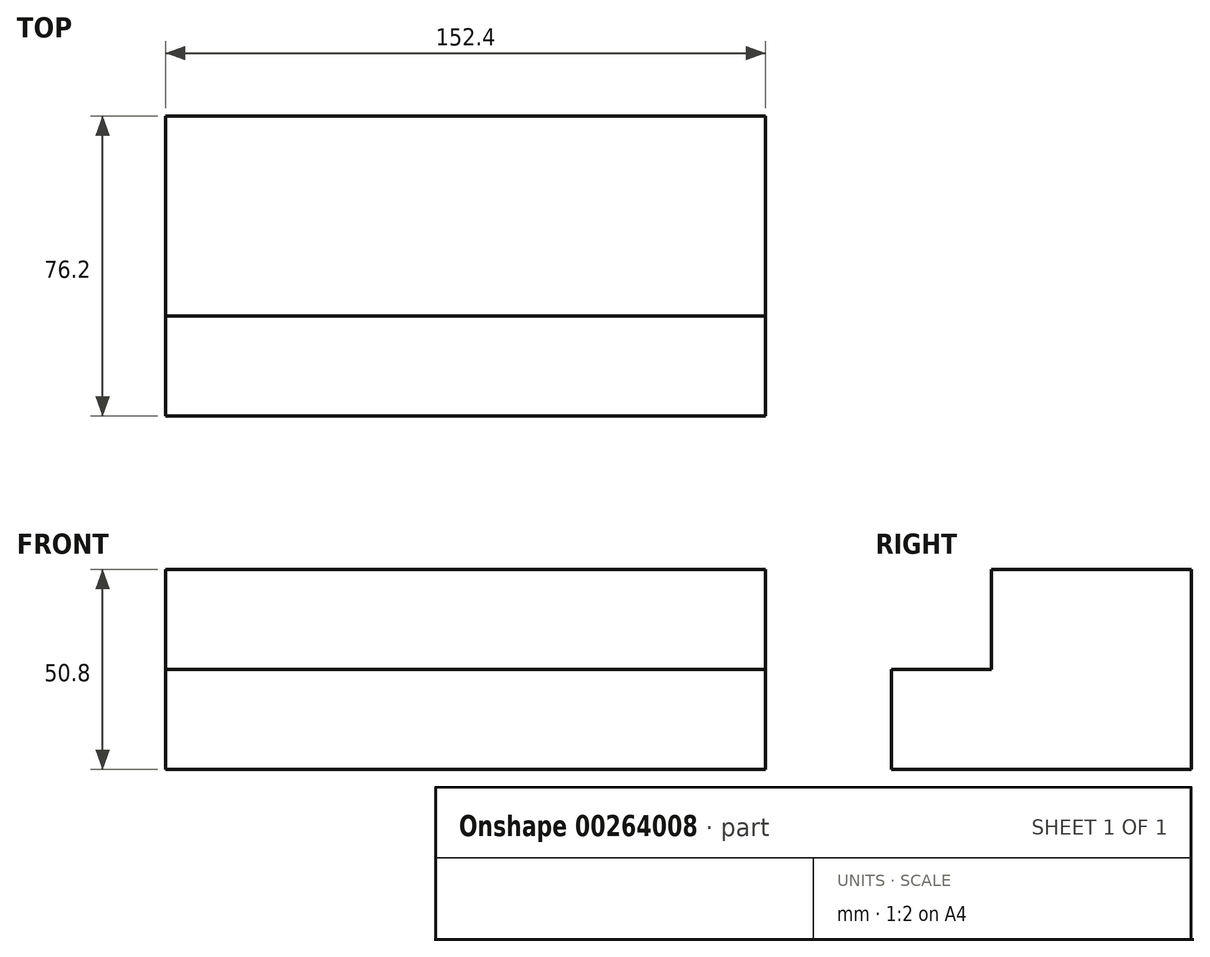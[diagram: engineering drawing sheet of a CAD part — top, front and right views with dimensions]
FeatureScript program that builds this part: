
annotation { "Feature Type Name" : "Feature", "Feature Type Description" : "" }
export const myFeature = defineFeature(function(context is Context, id is Id, definition is map)
    precondition{}
    {
        {
            var Q0;
            Q0=qCreatedBy(makeId("Right.planeOp"),FACE);
            var sketch = newSketch(context, id + "F0", { "sketchPlane" : qUnion([Q0])});
            skLineSegment(sketch, "E0", {"start": v(0, 0) * mm, "end": v(50.8, 0) * mm});
            skLineSegment(sketch, "E1", {"start": v(50.8, 0) * mm, "end": v(50.8, -50.8) * mm});
            skLineSegment(sketch, "E2", {"start": v(50.8, -50.8) * mm, "end": v(0, -50.8) * mm});
            skLineSegment(sketch, "E3", {"start": v(0, -50.8) * mm, "end": v(-25.4, -50.8) * mm});
            skLineSegment(sketch, "E4", {"start": v(-25.4, -50.8) * mm, "end": v(-25.4, -25.4) * mm});
            skLineSegment(sketch, "E5", {"start": v(-25.4, -25.4) * mm, "end": v(0, -25.4) * mm});
            skLineSegment(sketch, "E6", {"start": v(0, -25.4) * mm, "end": v(0, 0) * mm});
            skSolve(sketch);
        }
        {
            var Q0;
            Q0=makeQuery(id+"F0.imprint","IMPRINT",FACE,{"disambiguationData":[TD([[makeQuery(id+"F0.imprint","IMPRINT",EDGE,{"derivedFrom":sQuery(id+"F0.wireOp",EDGE,"E0")}),-1.0]])]});
            extrude(context, id + "F1", {"entities" : qUnion([Q0]), "depth" : 152.4 * mm});
        }
    });
